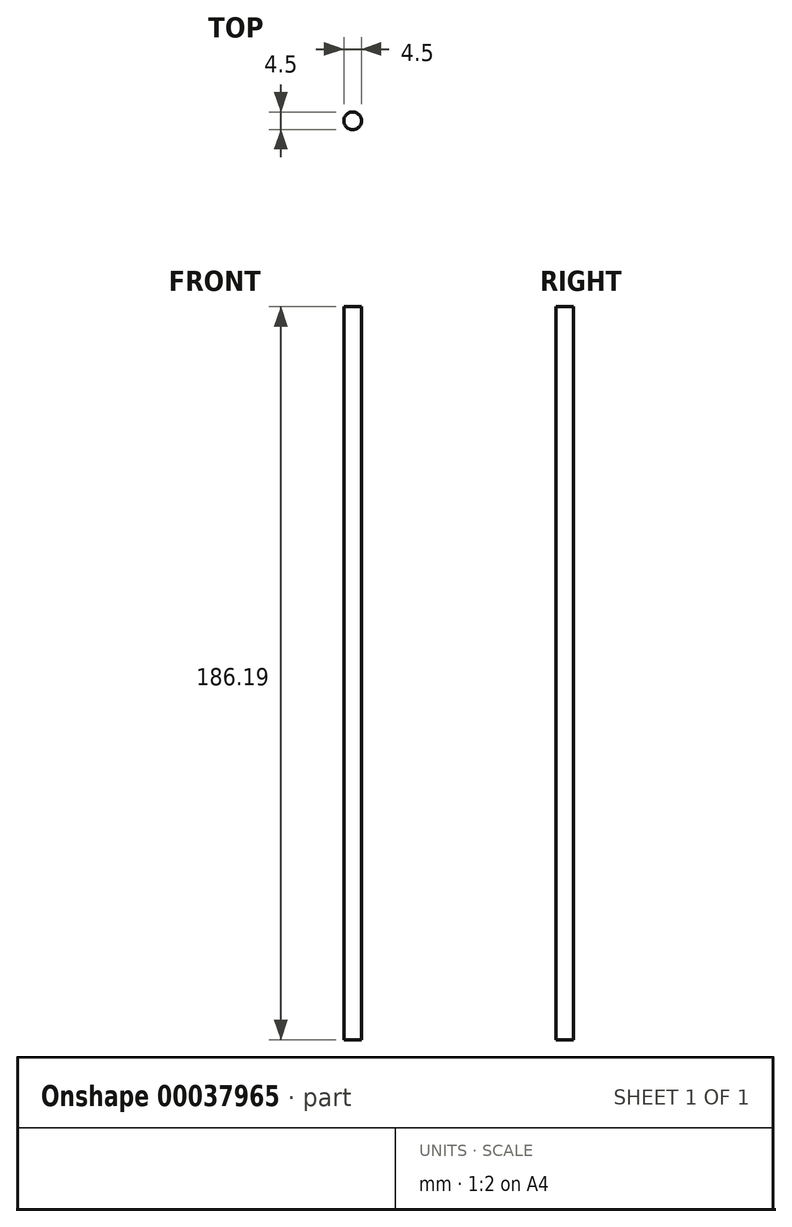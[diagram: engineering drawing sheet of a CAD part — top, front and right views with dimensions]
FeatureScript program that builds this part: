
annotation { "Feature Type Name" : "Feature", "Feature Type Description" : "" }
export const myFeature = defineFeature(function(context is Context, id is Id, definition is map)
    precondition{}
    {
        {
            var Q0;
            Q0=qCreatedBy(makeId("Top.planeOp"),FACE);
            var sketch = newSketch(context, id + "F0", { "sketchPlane" : qUnion([Q0])});
            skCircle(sketch, "E0", {"center": v(0, 0) * mm, "radius": 2.25 * mm});
            skSolve(sketch);
        }
        {
            var Q0;
            Q0=qSketchRegion(id+"F0",true);
            extrude(context, id + "F1", {"entities" : qUnion([Q0]), "depth" : 186.2 * mm});
        }
    });
